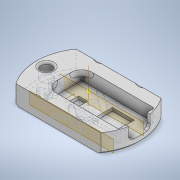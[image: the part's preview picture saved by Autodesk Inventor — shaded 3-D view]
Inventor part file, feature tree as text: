
AUTODESK INVENTOR PART (.ipt)
format: ipt  version: 2021 (Build 250183000, 183)  size: 598,528 bytes
history: native  units: in
note: dims shown in document units (in); Inventor stores cm internally (conversion verified against a paired STEP export)
features: sketch x11, extrude x9, fillet x4, plane x3, mirror x2, chamfer x1, other x1, pattern_circular x1
ambient origin geometry x8: Origin, YZ Plane, XZ Plane, XY Plane, X Axis, Y Axis, Z Axis, Center Point
bodies: Solid1 (feature_tree)
feature tree (32):
  extrude  "Extrusion1"  Depth=0.3701in TaperAngle=0.0deg
  chamfer  "Chamfer2"  Distance=0.2441in
  extrude  "Extrusion2"  Depth=0.1417in
  extrude  "Extrusion3"  Depth=0.2205in
  other  "Work Axis1"
  plane  "Work Plane1"
  extrude  "Extrusion4"  Depth=0.8268in
  fillet  "Fillet4"  Radius=0.3539in
  pattern_circular  "Circular Pattern2"  Angle=45.0deg  [1 undecoded]
  fillet  "Fillet7"  Radius=0.0394in
  extrude  "Initals"  Depth=0.063in TaperAngle=240.0deg
  fillet  "Fillet9"  Radius=0.0315in
  fillet  "Fillet10"  Radius=1.1811in
  mirror  "Mirror6"
  sketch  "Sketch18"  dims[d15=0.0in d16=0.0in d17=0.2205in]
  plane  "Work Plane5"
  extrude  "Extrusion13"  Depth=0.063in
  mirror  "Mirror7"
  extrude  "Extrusion15"  Depth=0.063in
  extrude  "Extrusion16"  Depth=0.063in
  plane  "Work Plane7"
  extrude  "Extrusion17"  Depth=0.063in TaperAngle=0.0deg
  sketch  "Sketch1"  dims[d0=2.0472in d3=0.3701in d4=0.0in]
  sketch  "Sketch2"  dims[d5=1.4315in]
  sketch  "Sketch3"  dims[d6=0.7079in]
  sketch  "Sketch4"  dims[d7=0.3539in]
  sketch  "Sketch12"  dims[d8=0.4882in d9=0.2441in d10=0.0in]
  sketch  "Sketch13"  dims[d11=0.0in d14=0.1417in]
  sketch  "Sketch19"  dims[d18=0.2047in d19=0.0in d23=0.8268in d24=0.3539in]
  sketch  "Sketch22"  dims[d44=0.1417in]
  sketch  "Sketch23"  dims[d47=0.0in]
  sketch  "Sketch24"  dims[d48=0.0in d49=0.0in d51=0.0in d54=0.0394in d55=0.0in d56=45.0deg d58=0.0394in d59=0.1181in d60=1.9685in d61=240.0deg d72=0.0315in d80=1.1811in d81=0.5906in d82=0.9728in d83=0.4864in d84=0.0394in d85=0.0in d86=0.547in d87=0.2735in d88=0.0787in d89=0.0in d90=0.0787in d101=0.2362in d102=0.0315in d103=0.0315in d104=0.2953in d105=0.1575in d106=0.1969in d114=0.5906in d115=0.0in d116=0.0in d120=0.1772in d121=0.1772in d123=0.2362in d124=0.5354in d126=0.1575in d127=0.1575in d128=0.063in d129=0.0in d130=0.4331in d131=0.3937in d132=0.2362in d133=0.1969in d134=0.0in d135=0.0in d136=-0.0787in d137=0.0in d138=0.0in d139=0.2362in d140=0.0787in d91=0.0197in d92=0.0344in d93=0.0197in d94=0.0344in d122=0.0197in]
note: 1 required parameter value undecoded (feature->parameter linkage not recoverable at this tier; creation-order binding heuristic only, values carry confidence <= 0.55)
